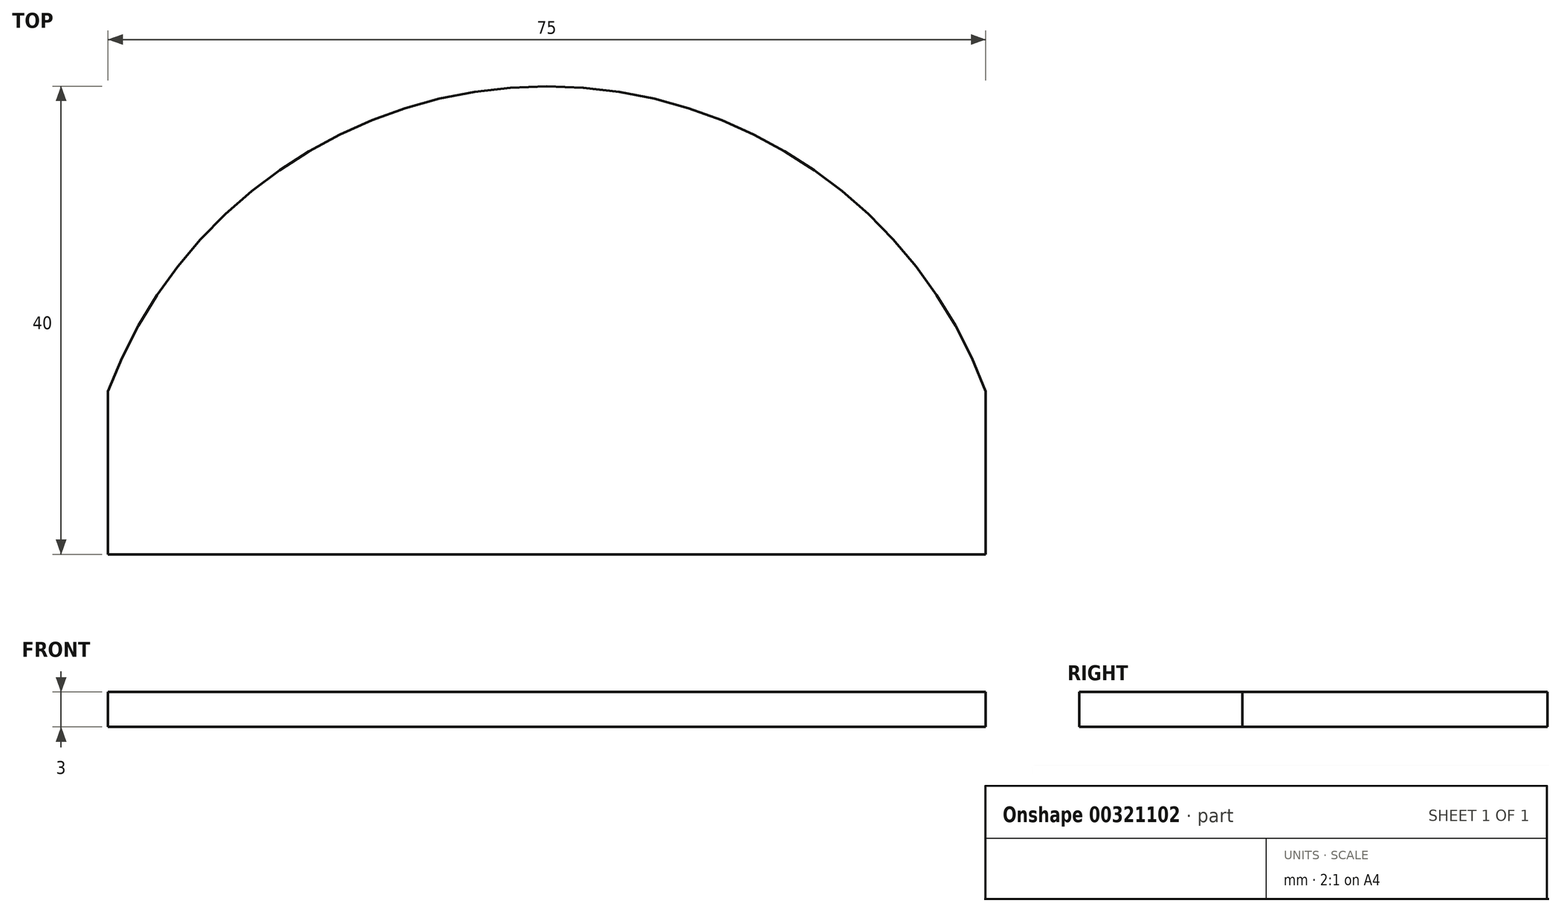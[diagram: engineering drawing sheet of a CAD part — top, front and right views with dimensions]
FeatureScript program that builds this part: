
annotation { "Feature Type Name" : "Feature", "Feature Type Description" : "" }
export const myFeature = defineFeature(function(context is Context, id is Id, definition is map)
    precondition{}
    {
        {
            var Q0;
            Q0=qCreatedBy(makeId("Top.planeOp"),FACE);
            var sketch = newSketch(context, id + "F0", { "sketchPlane" : qUnion([Q0])});
            skArc(sketch, "E0", {"start": v(37.5, 13.92) * mm, "mid": v(0, 40) * mm, "end": v(-37.5, 13.92) * mm});
            skLineSegment(sketch, "E1.top", {"start": v(37.5, 13.92) * mm, "end": v(-37.5, 13.92) * mm, "construction": true});
            skLineSegment(sketch, "E1.left", {"start": v(37.5, 0) * mm, "end": v(37.5, 13.92) * mm});
            skLineSegment(sketch, "E1.right", {"start": v(-37.5, 0) * mm, "end": v(-37.5, 13.92) * mm});
            skLineSegment(sketch, "E2", {"start": v(-37.5, 0) * mm, "end": v(37.5, 0) * mm});
            skSolve(sketch);
        }
        {
            var Q0;
            Q0=makeQuery(id+"F0.imprint","IMPRINT",FACE,{"disambiguationData":[TD([[makeQuery(id+"F0.imprint","IMPRINT",EDGE,{"derivedFrom":sQuery(id+"F0.wireOp",EDGE,"E0")}),1.0]])]});
            extrude(context, id + "F1", {"entities" : qUnion([Q0]), "depth" : 3 * mm});
        }
    });
